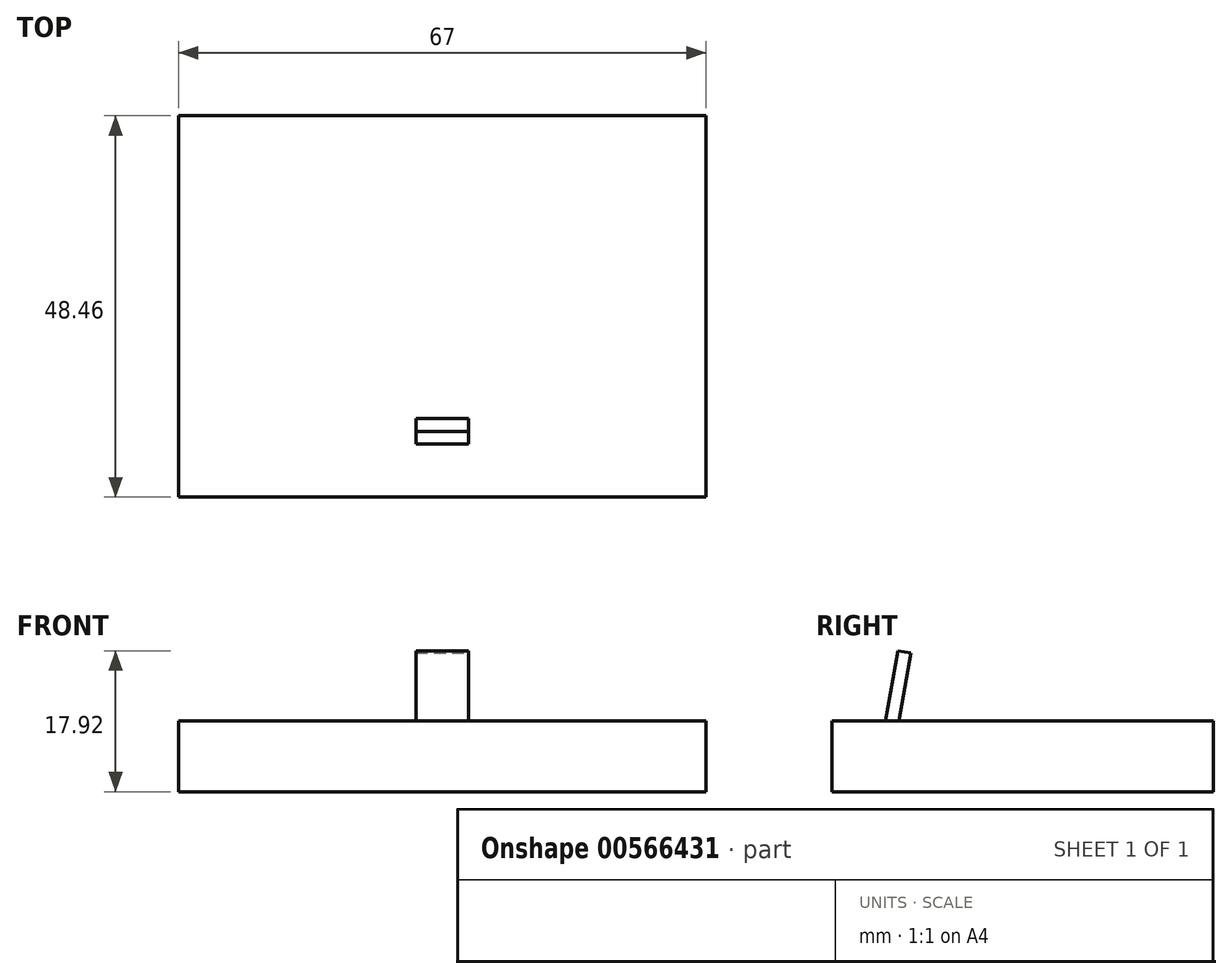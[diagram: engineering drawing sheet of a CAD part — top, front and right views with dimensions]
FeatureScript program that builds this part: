
annotation { "Feature Type Name" : "Feature", "Feature Type Description" : "" }
export const myFeature = defineFeature(function(context is Context, id is Id, definition is map)
    precondition{}
    {
        {
            var Q0;
            Q0=qCreatedBy(makeId("Top.planeOp"),FACE);
            var sketch = newSketch(context, id + "F0", { "sketchPlane" : qUnion([Q0])});
            skLineSegment(sketch, "E0.bottom", {"start": v(33.5, -24.23) * mm, "end": v(-33.5, -24.23) * mm});
            skLineSegment(sketch, "E0.top", {"start": v(33.5, 24.23) * mm, "end": v(-33.5, 24.23) * mm});
            skLineSegment(sketch, "E0.left", {"start": v(33.5, -24.23) * mm, "end": v(33.5, 24.23) * mm});
            skLineSegment(sketch, "E0.right", {"start": v(-33.5, -24.23) * mm, "end": v(-33.5, 24.23) * mm});
            skPoint(sketch, "E0.middle", {"position": v(0, 0) * mm});
            skSolve(sketch);
        }
        {
            var Q0;
            Q0=makeQuery(id+"F0.imprint","IMPRINT",FACE,{"disambiguationData":[TD([[makeQuery(id+"F0.imprint","IMPRINT",EDGE,{"derivedFrom":sQuery(id+"F0.wireOp",EDGE,"E0.bottom")}),-1.0]])]});
            extrude(context, id + "F1", {"entities" : qUnion([Q0]), "depth" : 9 * mm, "offsetDistance" : 25 * mm});
        }
        {
            var Q0;
            Q0=makeQuery(id+"F1.opExtrude","SWEPT_FACE",FACE,{"disambiguationData":[OSD([sQuery(id+"F0.wireOp",EDGE,"E0.left")])]});
            var sketch = newSketch(context, id + "F2", { "sketchPlane" : qUnion([Q0])});
            skLineSegment(sketch, "E1", {"start": v(-17.44, 9) * mm, "end": v(-15.87, 17.92) * mm});
            skLineSegment(sketch, "E2", {"start": v(-15.87, 17.92) * mm, "end": v(-14.23, 17.63) * mm});
            skLineSegment(sketch, "E3", {"start": v(-14.23, 17.63) * mm, "end": v(-15.75, 9) * mm});
            skLineSegment(sketch, "E4", {"start": v(-15.75, 9) * mm, "end": v(-17.44, 9) * mm});
            skSolve(sketch);
        }
        {
            var Q0;
            Q0=makeQuery(id+"F2.imprint","IMPRINT",FACE,{"disambiguationData":[TD([[makeQuery(id+"F2.imprint","IMPRINT",EDGE,{"derivedFrom":sQuery(id+"F2.wireOp",EDGE,"E1")}),-1.0]])]});
            var Q1;
            Q1=makeQuery(id+"F1.opExtrude","SWEPT_FACE",FACE,{"disambiguationData":[OSD([sQuery(id+"F0.wireOp",EDGE,"E0.right")])]});
            extrude(context, id + "F3", {"entities" : qUnion([Q0]), "endBound" : BoundingType.UP_TO_SURFACE, "oppositeDirection" : true, "depth" : 25 * mm, "endBoundEntityFace" : qUnion([Q1]), "offsetDistance" : 25 * mm});
        }
        {
            var Q0;
            Q0=makeQuery(id+"F1.opExtrude","SWEPT_FACE",FACE,{"disambiguationData":[OSD([sQuery(id+"F0.wireOp",EDGE,"E0.bottom")])]});
            var sketch = newSketch(context, id + "F4", { "sketchPlane" : qUnion([Q0])});
            skLineSegment(sketch, "E5.bottom", {"start": v(3.35, 9) * mm, "end": v(-3.35, 9) * mm});
            skLineSegment(sketch, "E5.top", {"start": v(3.35, 17.92) * mm, "end": v(-3.35, 17.92) * mm});
            skLineSegment(sketch, "E5.left", {"start": v(3.35, 9) * mm, "end": v(3.35, 17.92) * mm});
            skLineSegment(sketch, "E5.right", {"start": v(-3.35, 9) * mm, "end": v(-3.35, 17.92) * mm});
            skPoint(sketch, "E5.middle", {"position": v(0, 13.46) * mm});
            skPoint(sketch, "E6", {"position": v(0, 9) * mm});
            skSolve(sketch);
        }
        {
            var Q0;
            Q0=qSketchRegion(id+"F4",true);
            var Q1;
            Q1=makeQuery(id+"F1.opExtrude","SWEPT_FACE",FACE,{"disambiguationData":[OSD([sQuery(id+"F0.wireOp",EDGE,"E0.top")])]});
            extrude(context, id + "F5", {"entities" : qUnion([Q0]), "endBound" : BoundingType.UP_TO_SURFACE, "oppositeDirection" : true, "depth" : 25 * mm, "endBoundEntityFace" : qUnion([Q1]), "offsetDistance" : 25 * mm});
        }
        {
            var Q0;
            Q0=makeQuery(id+"F3.opExtrude","SWEPT_BODY",BODY,{"disambiguationData":[OSD([sQuery(id+"F2.wireOp",EDGE,"E1"),sQuery(id+"F2.wireOp",EDGE,"E2"),sQuery(id+"F2.wireOp",EDGE,"E3"),sQuery(id+"F2.wireOp",EDGE,"E4")])]});
            var Q1;
            Q1=makeQuery(id+"F5.opExtrude","SWEPT_BODY",BODY,{"disambiguationData":[OSD([sQuery(id+"F4.wireOp",EDGE,"E5.bottom"),sQuery(id+"F4.wireOp",EDGE,"E5.top"),sQuery(id+"F4.wireOp",EDGE,"E5.left"),sQuery(id+"F4.wireOp",EDGE,"E5.right")])]});
            booleanBodies(context, id + "F6", {"operationType" : BooleanOperationType.INTERSECTION, "tools" : qUnion([Q0, Q1])});
        }
    });
